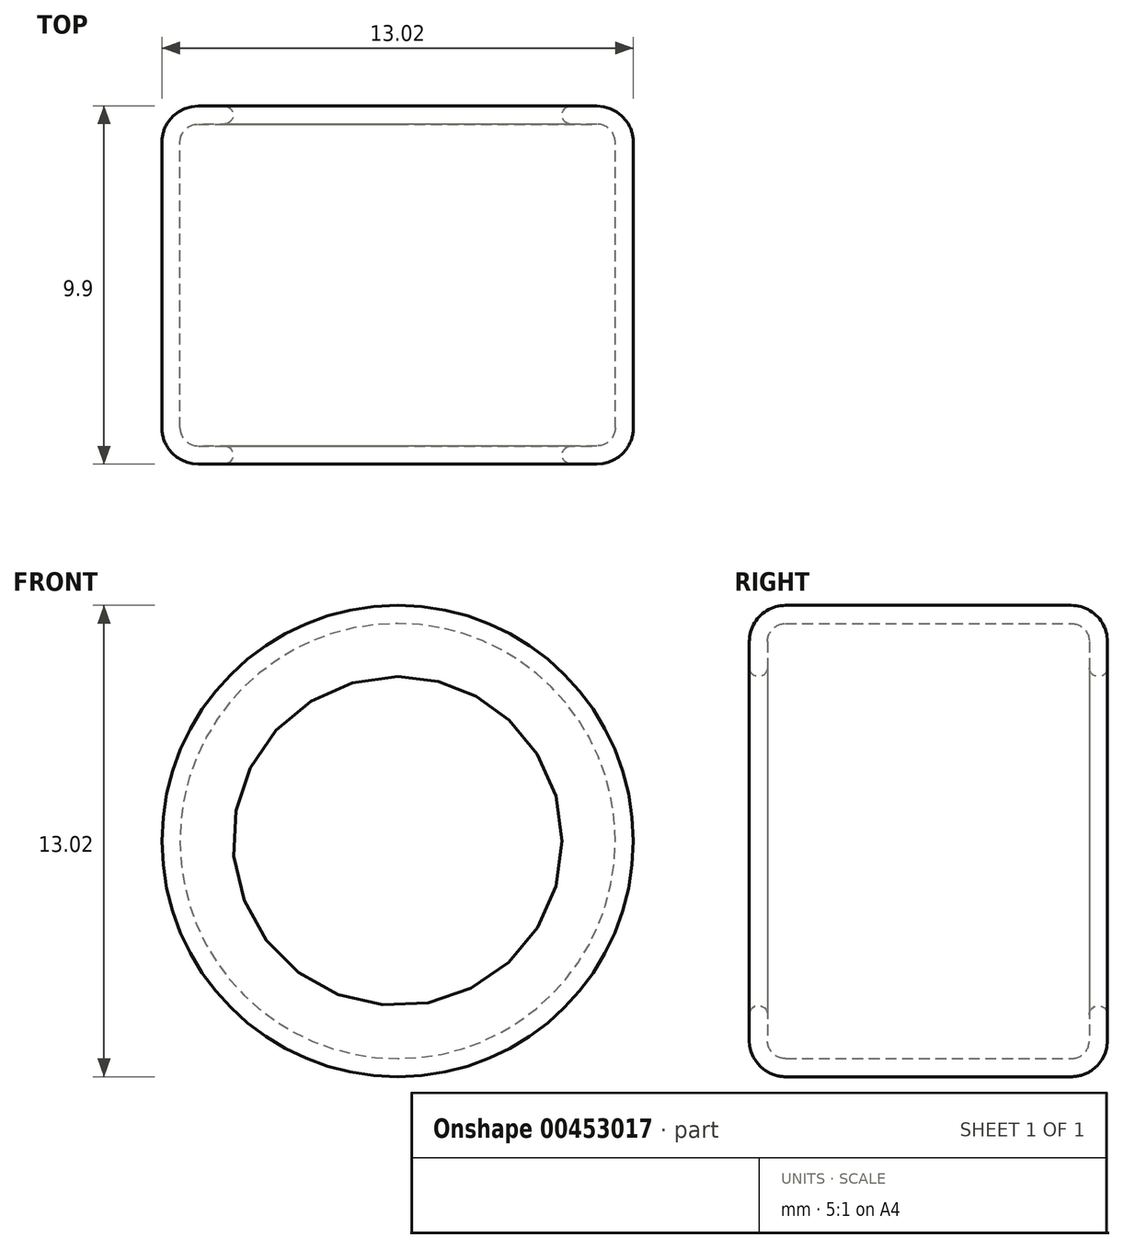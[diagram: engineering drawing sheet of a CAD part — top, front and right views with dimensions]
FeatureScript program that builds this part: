
annotation { "Feature Type Name" : "Feature", "Feature Type Description" : "" }
export const myFeature = defineFeature(function(context is Context, id is Id, definition is map)
    precondition{}
    {
        {
            var Q0;
            Q0=qCreatedBy(makeId("Top.planeOp"),FACE);
            var sketch = newSketch(context, id + "F0", { "sketchPlane" : qUnion([Q0])});
            skLineSegment(sketch, "E0", {"start": v(-6.5, 3.95) * mm, "end": v(-6.5, 0) * mm});
            skLineSegment(sketch, "E1", {"start": v(-5.5, 4.95) * mm, "end": v(-4.8, 4.95) * mm});
            skPoint(sketch, "E2.visualSharp", {"position": v(-6.5, 4.95) * mm});
            skArc(sketch, "E2.filletArc", {"start": v(-5.5, 4.95) * mm, "mid": v(-6.22, 4.65) * mm, "end": v(-6.5, 3.95) * mm});
            skLineSegment(sketch, "E3", {"start": v(0, 0) * mm, "end": v(-6.5, 0) * mm, "construction": true});
            skLineSegment(sketch, "E4.0", {"start": v(-6, 3.95) * mm, "end": v(-6, 0) * mm});
            skArc(sketch, "E4.1", {"start": v(-5.5, 4.45) * mm, "mid": v(-5.86, 4.3) * mm, "end": v(-6, 3.95) * mm});
            skLineSegment(sketch, "E4.2", {"start": v(-5.5, 4.45) * mm, "end": v(-4.8, 4.45) * mm});
            skLineSegment(sketch, "E5", {"start": v(-4.8, 4.95) * mm, "end": v(-4.8, 4.45) * mm, "construction": true});
            skArc(sketch, "E6", {"start": v(-4.8, 4.95) * mm, "mid": v(-4.54, 4.7) * mm, "end": v(-4.8, 4.45) * mm});
            skLineSegment(sketch, "E7.MirrorCS", {"start": v(-6, -3.95) * mm, "end": v(-6, 0) * mm});
            skArc(sketch, "E8.MirrorCS", {"start": v(-5.5, -4.45) * mm, "mid": v(-5.86, -4.3) * mm, "end": v(-6, -3.95) * mm});
            skLineSegment(sketch, "E9.MirrorCS", {"start": v(-5.5, -4.45) * mm, "end": v(-4.8, -4.45) * mm});
            skArc(sketch, "E10.MirrorCS", {"start": v(-4.8, -4.95) * mm, "mid": v(-4.54, -4.7) * mm, "end": v(-4.8, -4.45) * mm});
            skLineSegment(sketch, "E11.MirrorCS", {"start": v(-5.5, -4.95) * mm, "end": v(-4.8, -4.95) * mm});
            skArc(sketch, "E12.MirrorCS", {"start": v(-5.5, -4.95) * mm, "mid": v(-6.22, -4.65) * mm, "end": v(-6.5, -3.95) * mm});
            skLineSegment(sketch, "E13.MirrorCS", {"start": v(-6.5, -3.95) * mm, "end": v(-6.5, 0) * mm});
            skLineSegment(sketch, "E14", {"start": v(0, 5.5) * mm, "end": v(0, -3.1) * mm, "construction": true});
            skSolve(sketch);
        }
        {
            var Q0;
            Q0 = qSketchRegion(id + "F0", true);
            var Q1;
            Q1 = qConstructionFilter(qBodyType(qCreatedBy(id + "F0" ,EDGE), BodyType.WIRE), ConstructionObject.NO);
            var Q2;
            Q2=sQuery(id+"F0.wireOp",EDGE,"E14");
            revolve(context, id + "F1", {"surfaceOperationType" : NewSurfaceOperationType.NEW, "entities" : qUnion([Q0]), "surfaceEntities" : qUnion([Q1]), "axis" : qUnion([Q2]), "revolveType" : RevolveType.FULL});
        }
    });
